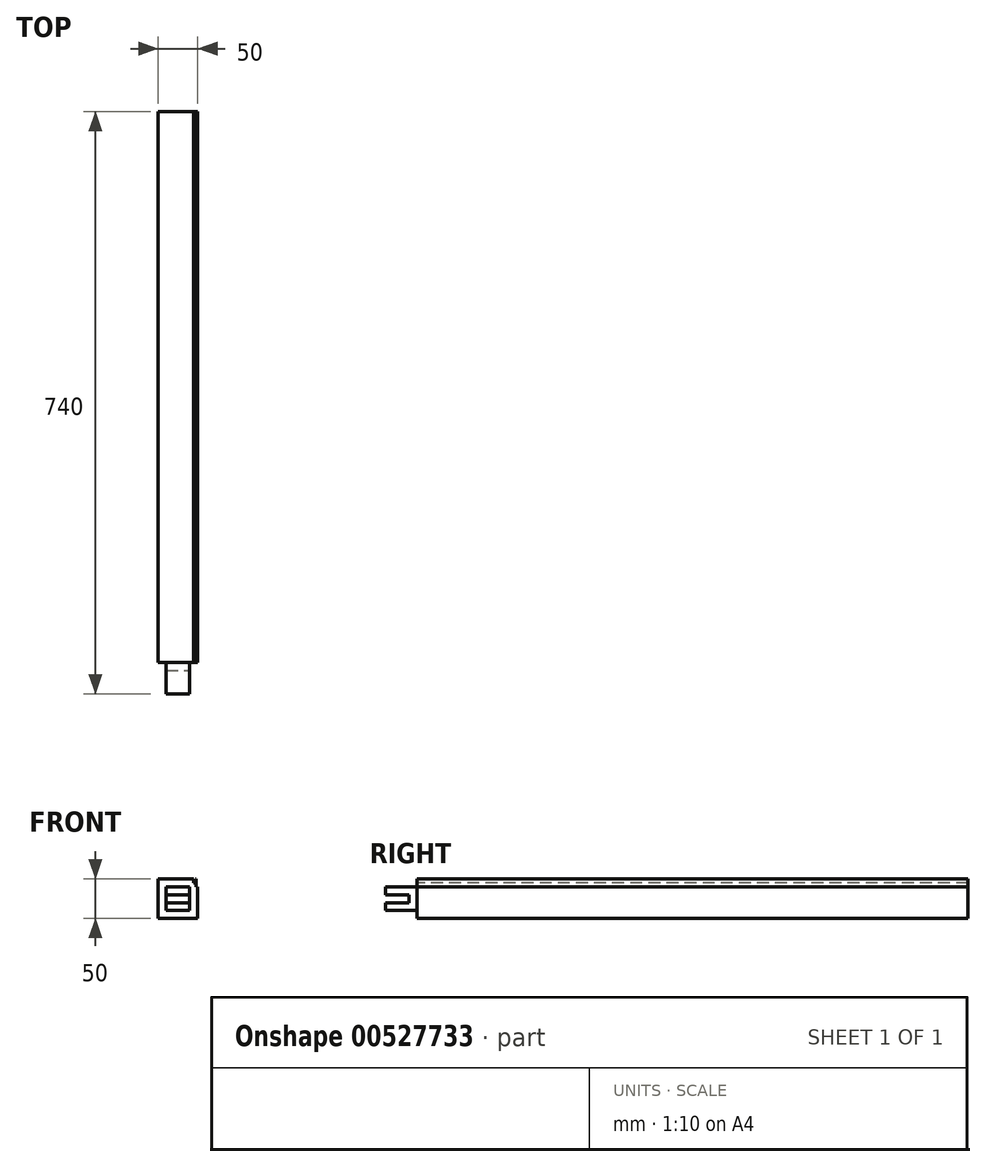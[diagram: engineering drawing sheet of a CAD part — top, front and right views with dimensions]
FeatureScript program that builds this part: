
annotation { "Feature Type Name" : "Feature", "Feature Type Description" : "" }
export const myFeature = defineFeature(function(context is Context, id is Id, definition is map)
    precondition{}
    {
        {
            var Q0;
            Q0=qCreatedBy(makeId("Front.planeOp"),FACE);
            var sketch = newSketch(context, id + "F0", { "sketchPlane" : qUnion([Q0])});
            skLineSegment(sketch, "E0.bottom", {"start": v(0, 0) * mm, "end": v(-50, 0) * mm});
            skLineSegment(sketch, "E0.top", {"start": v(0, 50) * mm, "end": v(-50, 50) * mm});
            skLineSegment(sketch, "E0.left", {"start": v(0, 0) * mm, "end": v(0, 50) * mm});
            skLineSegment(sketch, "E0.right", {"start": v(-50, 0) * mm, "end": v(-50, 50) * mm});
            skSolve(sketch);
        }
        {
            var Q0;
            Q0=makeQuery(id+"F0.imprint","IMPRINT",FACE,{"disambiguationData":[TD([[makeQuery(id+"F0.imprint","IMPRINT",EDGE,{"derivedFrom":sQuery(id+"F0.wireOp",EDGE,"E0.bottom")}),-1.0]])]});
            extrude(context, id + "F1", {"entities" : qUnion([Q0]), "depth" : 700 * mm, "offsetDistance" : 25 * mm});
        }
        {
            var Q0;
            Q0=makeQuery(id+"F1.opExtrude","CAP_FACE",FACE,{"disambiguationData":[OSD([sQuery(id+"F0.wireOp",EDGE,"E0.bottom"),sQuery(id+"F0.wireOp",EDGE,"E0.top"),sQuery(id+"F0.wireOp",EDGE,"E0.left"),sQuery(id+"F0.wireOp",EDGE,"E0.right")])],"isStart":false});
            cPlane(context, id + "F2", {"entities" : qUnion([Q0]), "cplaneType" : CPlaneType.OFFSET, "offset" : 350 * mm, "oppositeDirection" : true, "width" : 150 * mm, "height" : 150 * mm});
        }
        {
            var Q0;
            Q0=makeQuery(id+"F1.opExtrude","CAP_FACE",FACE,{"disambiguationData":[OSD([sQuery(id+"F0.wireOp",EDGE,"E0.bottom"),sQuery(id+"F0.wireOp",EDGE,"E0.top"),sQuery(id+"F0.wireOp",EDGE,"E0.left"),sQuery(id+"F0.wireOp",EDGE,"E0.right")])],"isStart":false});
            var sketch = newSketch(context, id + "F3", { "sketchPlane" : qUnion([Q0])});
            skLineSegment(sketch, "E1.bottom", {"start": v(-40, 40) * mm, "end": v(-10, 40) * mm});
            skLineSegment(sketch, "E1.top", {"start": v(-40, 10) * mm, "end": v(-10, 10) * mm});
            skLineSegment(sketch, "E1.left", {"start": v(-40, 40) * mm, "end": v(-40, 10) * mm});
            skLineSegment(sketch, "E1.right", {"start": v(-10, 40) * mm, "end": v(-10, 10) * mm});
            skSolve(sketch);
        }
        {
            var Q0;
            Q0=makeQuery(id+"F3.imprint","IMPRINT",FACE,{"disambiguationData":[TD([[makeQuery(id+"F3.imprint","IMPRINT",EDGE,{"derivedFrom":sQuery(id+"F3.wireOp",EDGE,"E1.bottom")}),-1.0]])]});
            extrude(context, id + "F4", {"entities" : qUnion([Q0]), "operationType" : NewBodyOperationType.ADD, "depth" : 40 * mm, "offsetDistance" : 25 * mm});
        }
        {
            var Q0;
            Q0=makeQuery(id+"F4.opExtrude","CAP_FACE",FACE,{"disambiguationData":[OSD([sQuery(id+"F3.wireOp",EDGE,"E1.bottom"),sQuery(id+"F3.wireOp",EDGE,"E1.top"),sQuery(id+"F3.wireOp",EDGE,"E1.left"),sQuery(id+"F3.wireOp",EDGE,"E1.right")])],"isStart":false});
            var sketch = newSketch(context, id + "F5", { "sketchPlane" : qUnion([Q0])});
            skLineSegment(sketch, "E2.bottom", {"start": v(-40, 30) * mm, "end": v(-10, 30) * mm});
            skLineSegment(sketch, "E2.top", {"start": v(-40, 20) * mm, "end": v(-10, 20) * mm});
            skLineSegment(sketch, "E2.left", {"start": v(-40, 30) * mm, "end": v(-40, 20) * mm});
            skLineSegment(sketch, "E2.right", {"start": v(-10, 30) * mm, "end": v(-10, 20) * mm});
            skSolve(sketch);
        }
        {
            var Q0;
            Q0=makeQuery(id+"F5.imprint","IMPRINT",FACE,{"disambiguationData":[TD([[makeQuery(id+"F5.imprint","IMPRINT",EDGE,{"derivedFrom":sQuery(id+"F5.wireOp",EDGE,"E2.bottom")}),-1.0]])]});
            extrude(context, id + "F6", {"entities" : qUnion([Q0]), "operationType" : NewBodyOperationType.REMOVE, "oppositeDirection" : true, "depth" : 30 * mm, "offsetDistance" : 25 * mm});
        }
        {
            var Q0;
            Q0=makeQuery(id+"F1.opExtrude","SWEPT_FACE",FACE,{"disambiguationData":[OSD([sQuery(id+"F0.wireOp",EDGE,"E0.left")])]});
            var sketch = newSketch(context, id + "F7", { "sketchPlane" : qUnion([Q0])});
            skLineSegment(sketch, "E3.bottom", {"start": v(-700, 50) * mm, "end": v(0, 50) * mm});
            skLineSegment(sketch, "E3.top", {"start": v(-700, 40) * mm, "end": v(0, 40) * mm});
            skLineSegment(sketch, "E3.left", {"start": v(-700, 50) * mm, "end": v(-700, 40) * mm});
            skLineSegment(sketch, "E3.right", {"start": v(0, 50) * mm, "end": v(0, 40) * mm});
            skSolve(sketch);
        }
        {
            var Q0;
            Q0 = qSketchRegion(id + "F7", true);
            extrude(context, id + "F8", {"entities" : qUnion([Q0]), "operationType" : NewBodyOperationType.REMOVE, "oppositeDirection" : true, "depth" : 2 * mm, "offsetDistance" : 25 * mm});
        }
        {
            var Q0;
            Q0=makeQuery(id+"F1.opExtrude","SWEPT_FACE",FACE,{"disambiguationData":[OSD([sQuery(id+"F0.wireOp",EDGE,"E0.top")])]});
            var sketch = newSketch(context, id + "F9", { "sketchPlane" : qUnion([Q0])});
            skLineSegment(sketch, "E4.bottom", {"start": v(-5, 0) * mm, "end": v(-3, 0) * mm});
            skLineSegment(sketch, "E4.top", {"start": v(-5, -700) * mm, "end": v(-3, -700) * mm});
            skLineSegment(sketch, "E4.left", {"start": v(-5, 0) * mm, "end": v(-5, -700) * mm});
            skLineSegment(sketch, "E4.right", {"start": v(-3, 0) * mm, "end": v(-3, -700) * mm});
            skSolve(sketch);
        }
        {
            var Q0;
            Q0 = qSketchRegion(id + "F9", true);
            extrude(context, id + "F10", {"entities" : qUnion([Q0]), "operationType" : NewBodyOperationType.REMOVE, "oppositeDirection" : true, "depth" : 5 * mm, "offsetDistance" : 25 * mm});
        }
    });
